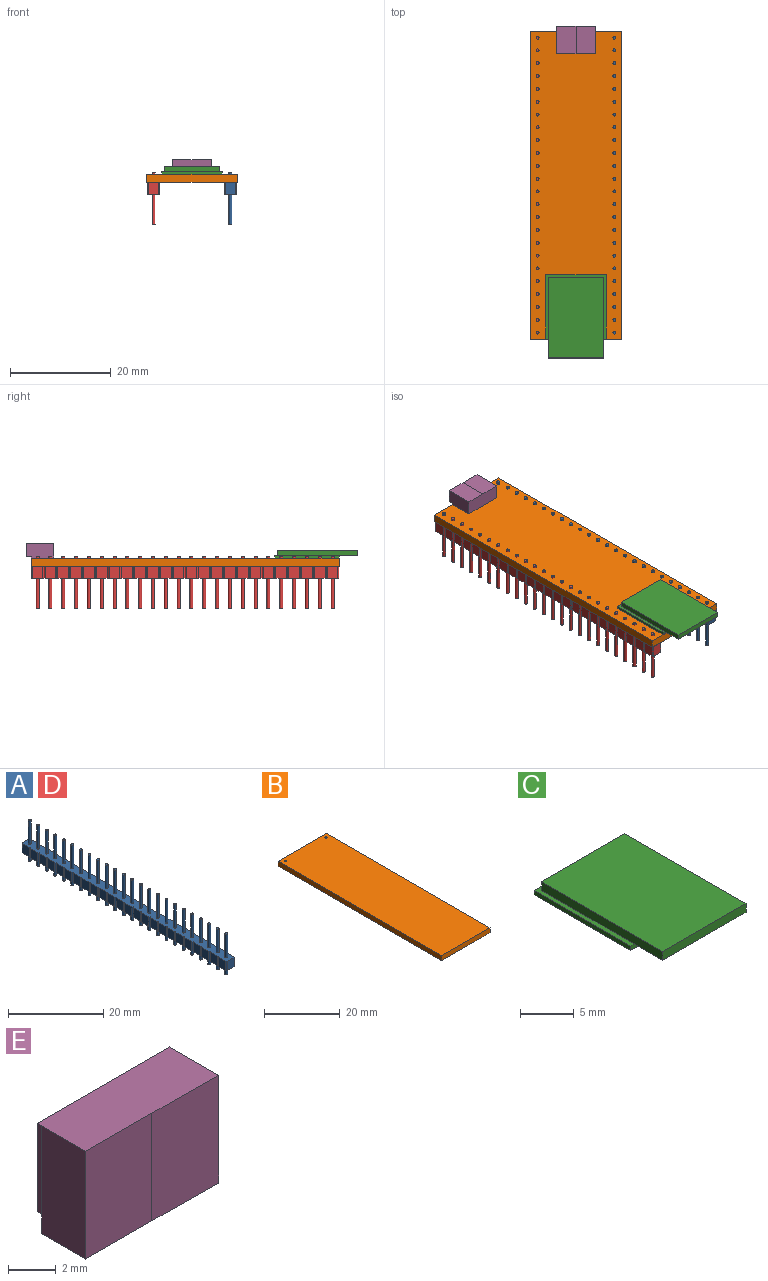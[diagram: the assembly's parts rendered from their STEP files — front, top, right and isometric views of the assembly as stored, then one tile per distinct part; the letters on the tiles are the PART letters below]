
ASSEMBLY  parts=5 mates=4
PART A: 244 faces, bbox 2.4x61x10.4 mm
  f0: plane 2.4x0.21mm, normal (-0.72,-0.69,0), area 0.7mm2, adj f1,f145,f146,f147
  f1: plane 2.4x0.21mm, normal (-0.72,0.69,0), area 0.7mm2, adj f0,f2,f146,f147
  f2: plane 2.4x2.12mm, normal (-1,0,0), area 5.1mm2, adj f1,f3,f146,f147
  f3: plane 2.4x0.21mm, normal (-0.72,-0.69,0), area 0.7mm2, adj f2,f4,f146,f147
  f4: plane 2.4x0.21mm, normal (-0.72,0.69,0), area 0.7mm2, adj f3,f5,f146,f147
  f5: plane 2.4x2.12mm, normal (-1,0,0), area 5.1mm2, adj f4,f6,f146,f147
  f6: plane 2.4x0.21mm, normal (-0.72,-0.69,0), area 0.7mm2, adj f5,f7,f146,f147
  f7: plane 2.4x0.21mm, normal (-0.72,0.69,0), area 0.7mm2, adj f6,f8,f146,f147
  f8: plane 2.4x2.12mm, normal (-1,0,0), area 5.1mm2, adj f7,f9,f146,f147
  f9: plane 2.4x0.21mm, normal (-0.72,-0.69,0), area 0.7mm2, adj f8,f10,f146,f147
  f10: plane 2.4x0.21mm, normal (-0.72,0.69,0), area 0.7mm2, adj f9,f11,f146,f147
  f11: plane 2.4x2.12mm, normal (-1,0,0), area 5.1mm2, adj f10,f12,f146,f147
  f12: plane 2.4x0.21mm, normal (-0.72,-0.69,0), area 0.7mm2, adj f11,f13,f146,f147
  f13: plane 2.4x0.21mm, normal (-0.72,0.69,0), area 0.7mm2, adj f12,f14,f146,f147
  f14: plane 2.4x2.12mm, normal (-1,0,0), area 5.1mm2, adj f13,f15,f146,f147
  f15: plane 2.4x0.21mm, normal (-0.72,-0.69,0), area 0.7mm2, adj f14,f16,f146,f147
  f16: plane 2.4x0.21mm, normal (-0.72,0.69,0), area 0.7mm2, adj f15,f17,f146,f147
  f17: plane 2.4x2.12mm, normal (-1,0,0), area 5.1mm2, adj f16,f18,f146,f147
  f18: plane 2.4x0.21mm, normal (-0.72,-0.69,0), area 0.7mm2, adj f17,f19,f146,f147
  f19: plane 2.4x0.21mm, normal (-0.72,0.69,0), area 0.7mm2, adj f18,f20,f146,f147
  f20: plane 2.4x2.12mm, normal (-1,0,0), area 5.1mm2, adj f19,f21,f146,f147
  f21: plane 2.4x0.21mm, normal (-0.72,-0.69,0), area 0.7mm2, adj f20,f22,f146,f147
  f22: plane 2.4x0.21mm, normal (-0.72,0.69,0), area 0.7mm2, adj f21,f23,f146,f147
  f23: plane 2.4x2.12mm, normal (-1,0,0), area 5.1mm2, adj f22,f24,f146,f147
  f24: plane 2.4x0.21mm, normal (-0.72,-0.69,0), area 0.7mm2, adj f23,f25,f146,f147
  f25: plane 2.4x0.21mm, normal (-0.72,0.69,0), area 0.7mm2, adj f24,f26,f146,f147
  f26: plane 2.4x2.12mm, normal (-1,0,0), area 5.1mm2, adj f25,f27,f146,f147
  f27: plane 2.4x0.21mm, normal (-0.72,-0.69,0), area 0.7mm2, adj f26,f28,f146,f147
  f28: plane 2.4x0.21mm, normal (-0.72,0.69,0), area 0.7mm2, adj f27,f29,f146,f147
  f29: plane 2.4x2.12mm, normal (-1,0,0), area 5.1mm2, adj f28,f30,f146,f147
  f30: plane 2.4x0.21mm, normal (-0.72,-0.69,0), area 0.7mm2, adj f29,f31,f146,f147
  f31: plane 2.4x0.21mm, normal (-0.72,0.69,0), area 0.7mm2, adj f30,f32,f146,f147
  f32: plane 2.4x2.12mm, normal (-1,0,0), area 5.1mm2, adj f31,f33,f146,f147
  f33: plane 2.4x0.21mm, normal (-0.72,-0.69,0), area 0.7mm2, adj f32,f34,f146,f147
  f34: plane 2.4x0.21mm, normal (-0.72,0.69,0), area 0.7mm2, adj f33,f35,f146,f147
  f35: plane 2.4x2.12mm, normal (-1,0,0), area 5.1mm2, adj f34,f36,f146,f147
  f36: plane 2.4x0.21mm, normal (-0.72,-0.69,0), area 0.7mm2, adj f35,f37,f146,f147
  f37: plane 2.4x0.21mm, normal (-0.72,0.69,0), area 0.7mm2, adj f36,f38,f146,f147
  f38: plane 2.4x2.12mm, normal (-1,0,0), area 5.1mm2, adj f37,f39,f146,f147
  f39: plane 2.4x0.21mm, normal (-0.72,-0.69,0), area 0.7mm2, adj f38,f40,f146,f147
  f40: plane 2.4x0.21mm, normal (-0.72,0.69,0), area 0.7mm2, adj f39,f41,f146,f147
  f41: plane 2.4x2.12mm, normal (-1,0,0), area 5.1mm2, adj f40,f42,f146,f147
  f42: plane 2.4x0.21mm, normal (-0.72,-0.69,0), area 0.7mm2, adj f41,f43,f146,f147
  f43: plane 2.4x0.21mm, normal (-0.72,0.69,0), area 0.7mm2, adj f42,f44,f146,f147
  f44: plane 2.4x2.12mm, normal (-1,0,0), area 5.1mm2, adj f43,f45,f146,f147
  f45: plane 2.4x0.21mm, normal (-0.72,-0.69,0), area 0.7mm2, adj f44,f46,f146,f147
  f46: plane 2.4x0.21mm, normal (-0.72,0.69,0), area 0.7mm2, adj f45,f47,f146,f147
  f47: plane 2.4x2.12mm, normal (-1,0,0), area 5.1mm2, adj f46,f48,f146,f147
  f48: plane 2.4x0.21mm, normal (-0.72,-0.69,0), area 0.7mm2, adj f47,f49,f146,f147
  f49: plane 2.4x0.21mm, normal (-0.72,0.69,0), area 0.7mm2, adj f48,f50,f146,f147
  f50: plane 2.4x2.12mm, normal (-1,0,0), area 5.1mm2, adj f49,f51,f146,f147
  f51: plane 2.4x0.21mm, normal (-0.72,-0.69,0), area 0.7mm2, adj f50,f52,f146,f147
  f52: plane 2.4x0.21mm, normal (-0.72,0.69,0), area 0.7mm2, adj f51,f53,f146,f147
  f53: plane 2.4x2.12mm, normal (-1,0,0), area 5.1mm2, adj f52,f54,f146,f147
  f54: plane 2.4x0.21mm, normal (-0.72,-0.69,0), area 0.7mm2, adj f53,f55,f146,f147
  f55: plane 2.4x0.21mm, normal (-0.72,0.69,0), area 0.7mm2, adj f54,f56,f146,f147
  f56: plane 2.4x2.12mm, normal (-1,0,0), area 5.1mm2, adj f55,f57,f146,f147
  f57: plane 2.4x0.21mm, normal (-0.72,-0.69,0), area 0.7mm2, adj f56,f58,f146,f147
  f58: plane 2.4x0.21mm, normal (-0.72,0.69,0), area 0.7mm2, adj f57,f59,f146,f147
  f59: plane 2.4x2.12mm, normal (-1,0,0), area 5.1mm2, adj f58,f60,f146,f147
  f60: plane 2.4x0.21mm, normal (-0.72,-0.69,0), area 0.7mm2, adj f59,f61,f146,f147
  f61: plane 2.4x0.21mm, normal (-0.72,0.69,0), area 0.7mm2, adj f60,f62,f146,f147
  f62: plane 2.4x2.12mm, normal (-1,0,0), area 5.1mm2, adj f61,f63,f146,f147
  f63: plane 2.4x0.21mm, normal (-0.72,-0.69,0), area 0.7mm2, adj f62,f64,f146,f147
  f64: plane 2.4x0.21mm, normal (-0.72,0.69,0), area 0.7mm2, adj f63,f65,f146,f147
  f65: plane 2.4x2.12mm, normal (-1,0,0), area 5.1mm2, adj f64,f66,f146,f147
  f66: plane 2.4x0.21mm, normal (-0.72,-0.69,0), area 0.7mm2, adj f65,f67,f146,f147
  f67: plane 2.4x0.21mm, normal (-0.72,0.69,0), area 0.7mm2, adj f66,f68,f146,f147
  f68: plane 2.4x2.12mm, normal (-1,0,0), area 5.1mm2, adj f67,f69,f146,f147
  f69: plane 2.4x0.21mm, normal (-0.72,-0.69,0), area 0.7mm2, adj f68,f70,f146,f147
  f70: plane 2.4x2mm, normal (0,-1,0), area 4.8mm2, adj f69,f71,f146,f147
  f71: plane 2.4x0.21mm, normal (0.72,-0.69,0), area 0.7mm2, adj f70,f72,f146,f147
  f72: plane 2.4x2.12mm, normal (1,0,0), area 5.1mm2, adj f71,f73,f146,f147
  f73: plane 2.4x0.21mm, normal (0.72,0.69,0), area 0.7mm2, adj f72,f74,f146,f147
  f74: plane 2.4x0.21mm, normal (0.72,-0.69,0), area 0.7mm2, adj f73,f75,f146,f147
  f75: plane 2.4x2.12mm, normal (1,0,0), area 5.1mm2, adj f74,f76,f146,f147
  f76: plane 2.4x0.21mm, normal (0.72,0.69,0), area 0.7mm2, adj f75,f77,f146,f147
  f77: plane 2.4x0.21mm, normal (0.72,-0.69,0), area 0.7mm2, adj f76,f78,f146,f147
  f78: plane 2.4x2.12mm, normal (1,0,0), area 5.1mm2, adj f77,f79,f146,f147
  f79: plane 2.4x0.21mm, normal (0.72,0.69,0), area 0.7mm2, adj f78,f80,f146,f147
  f80: plane 2.4x0.21mm, normal (0.72,-0.69,0), area 0.7mm2, adj f79,f81,f146,f147
  f81: plane 2.4x2.12mm, normal (1,0,0), area 5.1mm2, adj f80,f82,f146,f147
  f82: plane 2.4x0.21mm, normal (0.72,0.69,0), area 0.7mm2, adj f81,f83,f146,f147
  f83: plane 2.4x0.21mm, normal (0.72,-0.69,0), area 0.7mm2, adj f82,f84,f146,f147
  f84: plane 2.4x2.12mm, normal (1,0,0), area 5.1mm2, adj f83,f85,f146,f147
  f85: plane 2.4x0.21mm, normal (0.72,0.69,0), area 0.7mm2, adj f84,f86,f146,f147
  f86: plane 2.4x0.21mm, normal (0.72,-0.69,0), area 0.7mm2, adj f85,f87,f146,f147
  f87: plane 2.4x2.12mm, normal (1,0,0), area 5.1mm2, adj f86,f88,f146,f147
  f88: plane 2.4x0.21mm, normal (0.72,0.69,0), area 0.7mm2, adj f87,f89,f146,f147
  f89: plane 2.4x0.21mm, normal (0.72,-0.69,0), area 0.7mm2, adj f88,f90,f146,f147
  f90: plane 2.4x2.12mm, normal (1,0,0), area 5.1mm2, adj f89,f91,f146,f147
  f91: plane 2.4x0.21mm, normal (0.72,0.69,0), area 0.7mm2, adj f90,f92,f146,f147
  f92: plane 2.4x0.21mm, normal (0.72,-0.69,0), area 0.7mm2, adj f91,f93,f146,f147
  f93: plane 2.4x2.12mm, normal (1,0,0), area 5.1mm2, adj f92,f94,f146,f147
  f94: plane 2.4x0.21mm, normal (0.72,0.69,0), area 0.7mm2, adj f93,f95,f146,f147
  f95: plane 2.4x0.21mm, normal (0.72,-0.69,0), area 0.7mm2, adj f94,f96,f146,f147
  f96: plane 2.4x2.12mm, normal (1,0,0), area 5.1mm2, adj f95,f97,f146,f147
  f97: plane 2.4x0.21mm, normal (0.72,0.69,0), area 0.7mm2, adj f96,f98,f146,f147
  f98: plane 2.4x0.21mm, normal (0.72,-0.69,0), area 0.7mm2, adj f97,f99,f146,f147
  f99: plane 2.4x2.12mm, normal (1,0,0), area 5.1mm2, adj f98,f100,f146,f147
  f100: plane 2.4x0.21mm, normal (0.72,0.69,0), area 0.7mm2, adj f99,f101,f146,f147
  f101: plane 2.4x0.21mm, normal (0.72,-0.69,0), area 0.7mm2, adj f100,f102,f146,f147
  f102: plane 2.4x2.12mm, normal (1,0,0), area 5.1mm2, adj f101,f103,f146,f147
  f103: plane 2.4x0.21mm, normal (0.72,0.69,0), area 0.7mm2, adj f102,f104,f146,f147
  f104: plane 2.4x0.21mm, normal (0.72,-0.69,0), area 0.7mm2, adj f103,f105,f146,f147
  f105: plane 2.4x2.12mm, normal (1,0,0), area 5.1mm2, adj f104,f106,f146,f147
  f106: plane 2.4x0.21mm, normal (0.72,0.69,0), area 0.7mm2, adj f105,f107,f146,f147
  f107: plane 2.4x0.21mm, normal (0.72,-0.69,0), area 0.7mm2, adj f106,f108,f146,f147
  f108: plane 2.4x2.12mm, normal (1,0,0), area 5.1mm2, adj f107,f109,f146,f147
  f109: plane 2.4x0.21mm, normal (0.72,0.69,0), area 0.7mm2, adj f108,f110,f146,f147
  f110: plane 2.4x0.21mm, normal (0.72,-0.69,0), area 0.7mm2, adj f109,f111,f146,f147
  f111: plane 2.4x2.12mm, normal (1,0,0), area 5.1mm2, adj f110,f112,f146,f147
  f112: plane 2.4x0.21mm, normal (0.72,0.69,0), area 0.7mm2, adj f111,f113,f146,f147
  f113: plane 2.4x0.21mm, normal (0.72,-0.69,0), area 0.7mm2, adj f112,f114,f146,f147
  f114: plane 2.4x2.12mm, normal (1,0,0), area 5.1mm2, adj f113,f115,f146,f147
  f115: plane 2.4x0.21mm, normal (0.72,0.69,0), area 0.7mm2, adj f114,f116,f146,f147
  f116: plane 2.4x0.21mm, normal (0.72,-0.69,0), area 0.7mm2, adj f115,f117,f146,f147
  f117: plane 2.4x2.12mm, normal (1,0,0), area 5.1mm2, adj f116,f118,f146,f147
  f118: plane 2.4x0.21mm, normal (0.72,0.69,0), area 0.7mm2, adj f117,f119,f146,f147
  f119: plane 2.4x0.21mm, normal (0.72,-0.69,0), area 0.7mm2, adj f118,f120,f146,f147
  f120: plane 2.4x2.12mm, normal (1,0,0), area 5.1mm2, adj f119,f121,f146,f147
  f121: plane 2.4x0.21mm, normal (0.72,0.69,0), area 0.7mm2, adj f120,f122,f146,f147
  f122: plane 2.4x0.21mm, normal (0.72,-0.69,0), area 0.7mm2, adj f121,f123,f146,f147
  f123: plane 2.4x2.12mm, normal (1,0,0), area 5.1mm2, adj f122,f124,f146,f147
  f124: plane 2.4x0.21mm, normal (0.72,0.69,0), area 0.7mm2, adj f123,f125,f146,f147
  f125: plane 2.4x0.21mm, normal (0.72,-0.69,0), area 0.7mm2, adj f124,f126,f146,f147
  f126: plane 2.4x2.12mm, normal (1,0,0), area 5.1mm2, adj f125,f127,f146,f147
  f127: plane 2.4x0.21mm, normal (0.72,0.69,0), area 0.7mm2, adj f126,f128,f146,f147
  f128: plane 2.4x0.21mm, normal (0.72,-0.69,0), area 0.7mm2, adj f127,f129,f146,f147
  f129: plane 2.4x2.12mm, normal (1,0,0), area 5.1mm2, adj f128,f130,f146,f147
  f130: plane 2.4x0.21mm, normal (0.72,0.69,0), area 0.7mm2, adj f129,f131,f146,f147
  f131: plane 2.4x0.21mm, normal (0.72,-0.69,0), area 0.7mm2, adj f130,f132,f146,f147
  f132: plane 2.4x2.12mm, normal (1,0,0), area 5.1mm2, adj f131,f133,f146,f147
  f133: plane 2.4x0.21mm, normal (0.72,0.69,0), area 0.7mm2, adj f132,f134,f146,f147
  f134: plane 2.4x0.21mm, normal (0.72,-0.69,0), area 0.7mm2, adj f133,f135,f146,f147
  f135: plane 2.4x2.12mm, normal (1,0,0), area 5.1mm2, adj f134,f136,f146,f147
  f136: plane 2.4x0.21mm, normal (0.72,0.69,0), area 0.7mm2, adj f135,f137,f146,f147
  f137: plane 2.4x0.21mm, normal (0.72,-0.69,0), area 0.7mm2, adj f136,f138,f146,f147
  f138: plane 2.4x2.12mm, normal (1,0,0), area 5.1mm2, adj f137,f139,f146,f147
  f139: plane 2.4x0.21mm, normal (0.72,0.69,0), area 0.7mm2, adj f138,f140,f146,f147
  f140: plane 2.4x0.21mm, normal (0.72,-0.69,0), area 0.7mm2, adj f139,f141,f146,f147
  f141: plane 2.4x2.12mm, normal (1,0,0), area 5.1mm2, adj f140,f142,f146,f147
  f142: plane 2.4x0.21mm, normal (0.72,0.69,0), area 0.7mm2, adj f141,f143,f146,f147
  f143: plane 2.4x2mm, normal (0,1,0), area 4.8mm2, adj f142,f144,f146,f147
  f144: plane 2.4x0.21mm, normal (-0.72,0.69,0), area 0.7mm2, adj f143,f145,f146,f147
  f145: plane 2.4x2.12mm, normal (-1,0,0), area 5.1mm2, adj f0,f144,f146,f147
  f146: plane 60.96x2.4mm, normal (0,0,1), area 137.5mm2, adj f0,f1,f2,f3,f4,f5,f6,f7
  f147: plane 60.96x2.4mm, normal (0,0,-1), area 137.5mm2, adj f0,f1,f2,f3,f4,f5,f6,f7
  f148: plane 0.6x0.6mm, normal (0,0,-1), area 0.3mm2, adj f149
  f149: cylinder r=0.3mm len=2mm, axis (0,0,-1), area 3.8mm2, adj f147,f148
  f150: cylinder r=0.3mm len=6mm, axis (0,0,-1), area 11.3mm2, adj f146,f151
  f151: plane 0.6x0.6mm, normal (0,0,1), area 0.3mm2, adj f150
  f152: plane 0.6x0.6mm, normal (0,0,-1), area 0.3mm2, adj f153
  f153: cylinder r=0.3mm len=2mm, axis (0,0,-1), area 3.8mm2, adj f147,f152
  f154: cylinder r=0.3mm len=6mm, axis (0,0,-1), area 11.3mm2, adj f146,f155
  f155: plane 0.6x0.6mm, normal (0,0,1), area 0.3mm2, adj f154
  f156: plane 0.6x0.6mm, normal (0,0,-1), area 0.3mm2, adj f157
  f157: cylinder r=0.3mm len=2mm, axis (0,0,-1), area 3.8mm2, adj f147,f156
  f158: cylinder r=0.3mm len=6mm, axis (0,0,-1), area 11.3mm2, adj f146,f159
  f159: plane 0.6x0.6mm, normal (0,0,1), area 0.3mm2, adj f158
  f160: plane 0.6x0.6mm, normal (0,0,-1), area 0.3mm2, adj f161
  f161: cylinder r=0.3mm len=2mm, axis (0,0,-1), area 3.8mm2, adj f147,f160
  f162: cylinder r=0.3mm len=6mm, axis (0,0,-1), area 11.3mm2, adj f146,f163
  f163: plane 0.6x0.6mm, normal (0,0,1), area 0.3mm2, adj f162
  f164: plane 0.6x0.6mm, normal (0,0,-1), area 0.3mm2, adj f165
  f165: cylinder r=0.3mm len=2mm, axis (0,0,-1), area 3.8mm2, adj f147,f164
  f166: cylinder r=0.3mm len=6mm, axis (0,0,-1), area 11.3mm2, adj f146,f167
  f167: plane 0.6x0.6mm, normal (0,0,1), area 0.3mm2, adj f166
  f168: plane 0.6x0.6mm, normal (0,0,-1), area 0.3mm2, adj f169
  f169: cylinder r=0.3mm len=2mm, axis (0,0,-1), area 3.8mm2, adj f147,f168
  f170: cylinder r=0.3mm len=6mm, axis (0,0,-1), area 11.3mm2, adj f146,f171
  f171: plane 0.6x0.6mm, normal (0,0,1), area 0.3mm2, adj f170
  f172: plane 0.6x0.6mm, normal (0,0,-1), area 0.3mm2, adj f173
  f173: cylinder r=0.3mm len=2mm, axis (0,0,-1), area 3.8mm2, adj f147,f172
  f174: cylinder r=0.3mm len=6mm, axis (0,0,-1), area 11.3mm2, adj f146,f175
  f175: plane 0.6x0.6mm, normal (0,0,1), area 0.3mm2, adj f174
  f176: plane 0.6x0.6mm, normal (0,0,-1), area 0.3mm2, adj f177
  f177: cylinder r=0.3mm len=2mm, axis (0,0,-1), area 3.8mm2, adj f147,f176
  f178: cylinder r=0.3mm len=6mm, axis (0,0,-1), area 11.3mm2, adj f146,f179
  f179: plane 0.6x0.6mm, normal (0,0,1), area 0.3mm2, adj f178
  f180: plane 0.6x0.6mm, normal (0,0,-1), area 0.3mm2, adj f181
  f181: cylinder r=0.3mm len=2mm, axis (0,0,-1), area 3.8mm2, adj f147,f180
  f182: cylinder r=0.3mm len=6mm, axis (0,0,-1), area 11.3mm2, adj f146,f183
  f183: plane 0.6x0.6mm, normal (0,0,1), area 0.3mm2, adj f182
  f184: plane 0.6x0.6mm, normal (0,0,-1), area 0.3mm2, adj f185
  f185: cylinder r=0.3mm len=2mm, axis (0,0,-1), area 3.8mm2, adj f147,f184
  f186: cylinder r=0.3mm len=6mm, axis (0,0,-1), area 11.3mm2, adj f146,f187
  f187: plane 0.6x0.6mm, normal (0,0,1), area 0.3mm2, adj f186
  f188: plane 0.6x0.6mm, normal (0,0,-1), area 0.3mm2, adj f189
  f189: cylinder r=0.3mm len=2mm, axis (0,0,-1), area 3.8mm2, adj f147,f188
  f190: cylinder r=0.3mm len=6mm, axis (0,0,-1), area 11.3mm2, adj f146,f191
  f191: plane 0.6x0.6mm, normal (0,0,1), area 0.3mm2, adj f190
  f192: plane 0.6x0.6mm, normal (0,0,-1), area 0.3mm2, adj f193
  f193: cylinder r=0.3mm len=2mm, axis (0,0,-1), area 3.8mm2, adj f147,f192
  f194: cylinder r=0.3mm len=6mm, axis (0,0,-1), area 11.3mm2, adj f146,f195
  f195: plane 0.6x0.6mm, normal (0,0,1), area 0.3mm2, adj f194
  f196: plane 0.6x0.6mm, normal (0,0,-1), area 0.3mm2, adj f197
  f197: cylinder r=0.3mm len=2mm, axis (0,0,-1), area 3.8mm2, adj f147,f196
  f198: cylinder r=0.3mm len=6mm, axis (0,0,-1), area 11.3mm2, adj f146,f199
  f199: plane 0.6x0.6mm, normal (0,0,1), area 0.3mm2, adj f198
  f200: plane 0.6x0.6mm, normal (0,0,-1), area 0.3mm2, adj f201
  f201: cylinder r=0.3mm len=2mm, axis (0,0,-1), area 3.8mm2, adj f147,f200
  f202: cylinder r=0.3mm len=6mm, axis (0,0,-1), area 11.3mm2, adj f146,f203
  f203: plane 0.6x0.6mm, normal (0,0,1), area 0.3mm2, adj f202
  f204: plane 0.6x0.6mm, normal (0,0,-1), area 0.3mm2, adj f205
  f205: cylinder r=0.3mm len=2mm, axis (0,0,-1), area 3.8mm2, adj f147,f204
  f206: cylinder r=0.3mm len=6mm, axis (0,0,-1), area 11.3mm2, adj f146,f207
  f207: plane 0.6x0.6mm, normal (0,0,1), area 0.3mm2, adj f206
  f208: plane 0.6x0.6mm, normal (0,0,-1), area 0.3mm2, adj f209
  f209: cylinder r=0.3mm len=2mm, axis (0,0,-1), area 3.8mm2, adj f147,f208
  f210: cylinder r=0.3mm len=6mm, axis (0,0,-1), area 11.3mm2, adj f146,f211
  f211: plane 0.6x0.6mm, normal (0,0,1), area 0.3mm2, adj f210
  f212: plane 0.6x0.6mm, normal (0,0,-1), area 0.3mm2, adj f213
  f213: cylinder r=0.3mm len=2mm, axis (0,0,-1), area 3.8mm2, adj f147,f212
  f214: cylinder r=0.3mm len=6mm, axis (0,0,-1), area 11.3mm2, adj f146,f215
  f215: plane 0.6x0.6mm, normal (0,0,1), area 0.3mm2, adj f214
  f216: plane 0.6x0.6mm, normal (0,0,-1), area 0.3mm2, adj f217
  f217: cylinder r=0.3mm len=2mm, axis (0,0,-1), area 3.8mm2, adj f147,f216
  f218: cylinder r=0.3mm len=6mm, axis (0,0,-1), area 11.3mm2, adj f146,f219
  f219: plane 0.6x0.6mm, normal (0,0,1), area 0.3mm2, adj f218
  f220: plane 0.6x0.6mm, normal (0,0,-1), area 0.3mm2, adj f221
  f221: cylinder r=0.3mm len=2mm, axis (0,0,-1), area 3.8mm2, adj f147,f220
  f222: cylinder r=0.3mm len=6mm, axis (0,0,-1), area 11.3mm2, adj f146,f223
  f223: plane 0.6x0.6mm, normal (0,0,1), area 0.3mm2, adj f222
  f224: plane 0.6x0.6mm, normal (0,0,-1), area 0.3mm2, adj f225
  f225: cylinder r=0.3mm len=2mm, axis (0,0,-1), area 3.8mm2, adj f147,f224
  f226: cylinder r=0.3mm len=6mm, axis (0,0,-1), area 11.3mm2, adj f146,f227
  f227: plane 0.6x0.6mm, normal (0,0,1), area 0.3mm2, adj f226
  f228: plane 0.6x0.6mm, normal (0,0,-1), area 0.3mm2, adj f229
  f229: cylinder r=0.3mm len=2mm, axis (0,0,-1), area 3.8mm2, adj f147,f228
  f230: cylinder r=0.3mm len=6mm, axis (0,0,-1), area 11.3mm2, adj f146,f231
  f231: plane 0.6x0.6mm, normal (0,0,1), area 0.3mm2, adj f230
  f232: plane 0.6x0.6mm, normal (0,0,-1), area 0.3mm2, adj f233
  f233: cylinder r=0.3mm len=2mm, axis (0,0,-1), area 3.8mm2, adj f147,f232
  f234: cylinder r=0.3mm len=6mm, axis (0,0,-1), area 11.3mm2, adj f146,f235
  f235: plane 0.6x0.6mm, normal (0,0,1), area 0.3mm2, adj f234
  f236: plane 0.6x0.6mm, normal (0,0,-1), area 0.3mm2, adj f237
  f237: cylinder r=0.3mm len=2mm, axis (0,0,-1), area 3.8mm2, adj f147,f236
  f238: cylinder r=0.3mm len=6mm, axis (0,0,-1), area 11.3mm2, adj f146,f239
  f239: plane 0.6x0.6mm, normal (0,0,1), area 0.3mm2, adj f238
  f240: plane 0.6x0.6mm, normal (0,0,-1), area 0.3mm2, adj f241
  f241: cylinder r=0.3mm len=2mm, axis (0,0,-1), area 3.8mm2, adj f147,f240
  f242: cylinder r=0.3mm len=6mm, axis (0,0,-1), area 11.3mm2, adj f146,f243
  f243: plane 0.6x0.6mm, normal (0,0,1), area 0.3mm2, adj f242
PART B: 8 faces, bbox 18x61x1.6 mm
  f0: plane 61x1.6mm, normal (-1,0,0), area 97.6mm2, adj f1,f3,f4,f5
  f1: plane 18x1.6mm, normal (0,-1,0), area 28.8mm2, adj f0,f2,f4,f5
  f2: plane 61x1.6mm, normal (1,0,0), area 97.6mm2, adj f1,f3,f4,f5
  f3: plane 18x1.6mm, normal (0,1,0), area 28.8mm2, adj f0,f2,f4,f5
  f4: plane 61x18mm, normal (0,0,1), area 1097.4mm2, adj f0,f1,f2,f3,f6,f7
  f5: plane 61x18mm, normal (0,0,-1), area 1097.4mm2, adj f0,f1,f2,f3,f6,f7
  f6: cylinder r=0.3mm len=1.6mm, axis (0,0,1), area 3mm2, adj f4,f5
  f7: cylinder r=0.3mm len=1.6mm, axis (0,0,1), area 3mm2, adj f4,f5
PART C: 12 faces, bbox 12x16.5x1.5 mm
  f0: plane 11x1mm, normal (0,-1,0), area 11mm2, adj f1,f3,f4,f5
  f1: plane 16x1mm, normal (1,0,0), area 16mm2, adj f0,f2,f4,f5,f6
  f2: plane 11x1mm, normal (0,1,0), area 11mm2, adj f1,f3,f4,f6
  f3: plane 16x1mm, normal (-1,0,0), area 16mm2, adj f0,f2,f4,f5,f6
  f4: plane 16x11mm, normal (0,0,1), area 176mm2, adj f0,f1,f2,f3
  f5: plane 11x3.75mm, normal (0,0,-1), area 41.2mm2, adj f0,f1,f3,f7
  f6: plane 12.75x12mm, normal (0,0,1), area 18.3mm2, adj f1,f2,f3,f7,f8,f9,f10
  f7: plane 12x0.5mm, normal (0,-1,0), area 6mm2, adj f5,f6,f8,f10,f11
  f8: plane 12.75x0.5mm, normal (-1,0,0), area 6.4mm2, adj f6,f7,f9,f11
  f9: plane 12x0.5mm, normal (0,1,0), area 6mm2, adj f6,f8,f10,f11
  f10: plane 12.75x0.5mm, normal (1,0,0), area 6.4mm2, adj f6,f7,f9,f11
  f11: plane 12.75x12mm, normal (0,0,-1), area 153mm2, adj f7,f8,f9,f10
PART D: same geometry as A
PART E: 10 faces, bbox 7.8x2.9x5.5 mm
  f0: plane 7.8x1mm, normal (0,1,0), area 7.8mm2, adj f1,f4,f6,f7
  f1: plane 5.5x2.61mm, normal (-1,0,0), area 14.4mm2, adj f0,f2,f5,f6,f8
  f2: plane 5.5x3.9mm, normal (0,-1,0), area 21.5mm2, adj f1,f3,f5,f6
  f3: plane 5.5x3.9mm, normal (-0.01,-1,0), area 21.5mm2, adj f2,f4,f5,f6
  f4: plane 5.5x2.9mm, normal (1,0,0), area 15.7mm2, adj f0,f3,f5,f6,f7,f9
  f5: plane 7.8x2.9mm, normal (0,0,1), area 22.4mm2, adj f1,f2,f3,f4,f8,f9
  f6: plane 7.8x2.65mm, normal (0,0,-1), area 20.4mm2, adj f0,f1,f2,f3,f4
  f7: plane 7.8x0.25mm, normal (0,0,-1), area 1.9mm2, adj f0,f4,f8,f9
  f8: plane 4.5x0.25mm, normal (-1,0,0), area 1.1mm2, adj f1,f5,f7,f9
  f9: plane 7.8x4.5mm, normal (0,1,0), area 35.1mm2, adj f4,f5,f7,f8
PLACE A rot(axis=(0,1,0),180deg) t=(-1.66,-3.06,0.74)mm
PLACE B t=(-9.28,-4.33,0.74)mm
PLACE C t=(-9.28,-30.58,2.84)mm
PLACE D rot(axis=(0,1,0),180deg) t=(-16.9,-3.06,0.74)mm
PLACE E rot(axis=(0,-0.71,0.71),180deg) t=(-9.28,27.17,2.59)mm
MATE fastened C.f11 <-> B.f4  axis (0,0,-1) through (-9.28,-34.83,2.34)mm
MATE fastened A.f149 <-> B.f6  axis (0,0,1) through (-1.66,24.88,0.74)mm
MATE fastened D.f149 <-> B.f7  axis (0,0,1) through (-16.9,24.88,0.74)mm
MATE fastened E.f9 <-> B.f4  axis (0,0,-1) through (-9.28,26.17,2.34)mm
